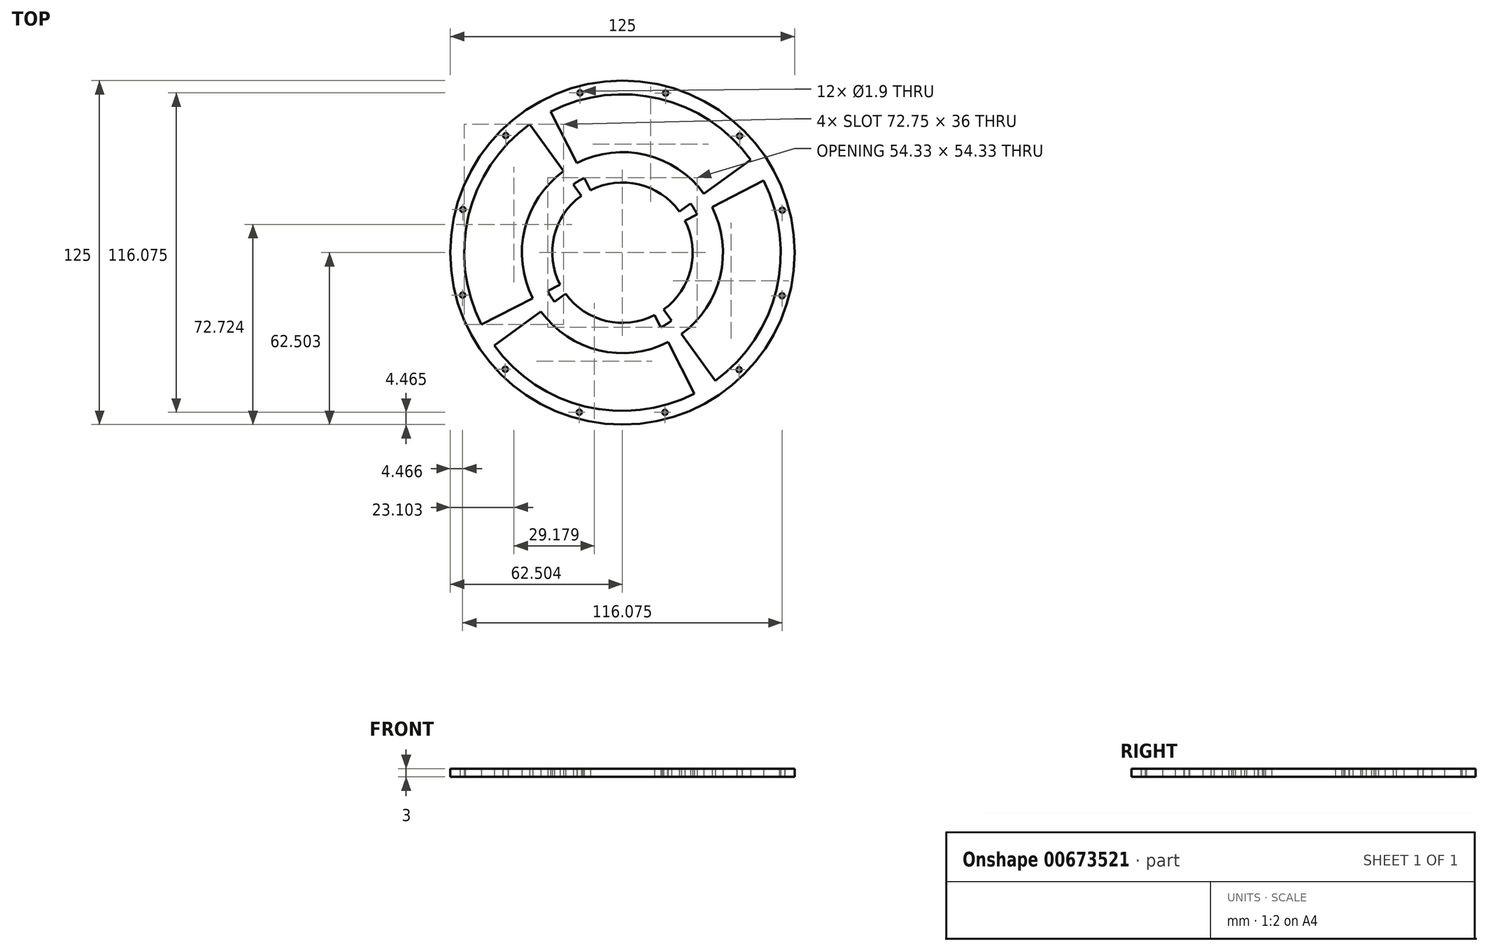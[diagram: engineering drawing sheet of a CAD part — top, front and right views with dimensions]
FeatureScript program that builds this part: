
annotation { "Feature Type Name" : "Feature", "Feature Type Description" : "" }
export const myFeature = defineFeature(function(context is Context, id is Id, definition is map)
    precondition{}
    {
        {
            var Q0;
            Q0=qCreatedBy(makeId("Top.planeOp"),FACE);
            var sketch = newSketch(context, id + "F0", { "sketchPlane" : qUnion([Q0])});
            skCircle(sketch, "E0", {"center": v(-11.5, 27.97) * mm, "radius": 25.5 * mm});
            skCircle(sketch, "E1.0", {"center": v(-11.5, 27.97) * mm, "radius": 30.5 * mm});
            skCircle(sketch, "E2", {"center": v(-11.5, 27.97) * mm, "radius": 57.5 * mm});
            skCircle(sketch, "E3.0", {"center": v(-11.5, 27.97) * mm, "radius": 62.5 * mm});
            skLineSegment(sketch, "E4", {"start": v(-11.5, 27.97) * mm, "end": v(39.71, 54.12) * mm});
            skLineSegment(sketch, "E5", {"start": v(-11.5, 27.97) * mm, "end": v(35.1, 61.67) * mm});
            skLineSegment(sketch, "E6.1.0", {"start": v(-11.5, 27.97) * mm, "end": v(-45.2, 74.57) * mm});
            skLineSegment(sketch, "E6.1.1", {"start": v(-11.5, 27.97) * mm, "end": v(-37.65, 79.18) * mm});
            skLineSegment(sketch, "E6.2.0", {"start": v(-11.5, 27.97) * mm, "end": v(-58.09, -5.72) * mm});
            skLineSegment(sketch, "E6.2.1", {"start": v(-11.5, 27.97) * mm, "end": v(-62.7, 1.82) * mm});
            skLineSegment(sketch, "E6.3.0", {"start": v(-11.5, 27.97) * mm, "end": v(22.2, -18.62) * mm});
            skLineSegment(sketch, "E6.3.1", {"start": v(-11.5, 27.97) * mm, "end": v(14.66, -23.24) * mm});
            skCircle(sketch, "E7", {"center": v(-11.5, 27.97) * mm, "radius": 36.52 * mm});
            skCircle(sketch, "E8", {"center": v(-27.16, -30) * mm, "radius": 0.95 * mm});
            skCircle(sketch, "E9.1.0", {"center": v(3.93, -30.06) * mm, "radius": 0.95 * mm});
            skCircle(sketch, "E9.2.0", {"center": v(30.88, -14.58) * mm, "radius": 0.95 * mm});
            skCircle(sketch, "E9.3.0", {"center": v(46.48, 12.31) * mm, "radius": 0.95 * mm});
            skCircle(sketch, "E9.4.0", {"center": v(46.54, 43.4) * mm, "radius": 0.95 * mm});
            skCircle(sketch, "E9.5.0", {"center": v(31.05, 70.35) * mm, "radius": 0.95 * mm});
            skCircle(sketch, "E9.6.0", {"center": v(4.17, 85.95) * mm, "radius": 0.95 * mm});
            skCircle(sketch, "E9.7.0", {"center": v(-26.92, 86.01) * mm, "radius": 0.95 * mm});
            skCircle(sketch, "E9.8.0", {"center": v(-53.87, 70.52) * mm, "radius": 0.95 * mm});
            skCircle(sketch, "E9.9.0", {"center": v(-69.47, 43.63) * mm, "radius": 0.95 * mm});
            skCircle(sketch, "E9.10.0", {"center": v(-69.53, 12.55) * mm, "radius": 0.95 * mm});
            skCircle(sketch, "E9.11.0", {"center": v(-54.05, -14.4) * mm, "radius": 0.95 * mm});
            skSolve(sketch);
        }
        {
            var Q0;
            Q0=qSketchRegion(id+"F0",true);
            var Q1;
            {var subQ0=sQuery(id+"F0.wireOp",EDGE,"E5");var subQ1=sQuery(id+"F0.wireOp",EDGE,"E0");var subQ2=makeQuery(id+"F0.imprint","INTERSECT",VERTEX,{"derivedFrom":[subQ1,subQ0]});Q1=makeQuery(id+"F0.imprint","IMPRINT",FACE,{"disambiguationData":[TD([[makeQuery(id+"F0.imprint","IMPRINT",EDGE,{"disambiguationData":[TD([[subQ2,-1.0]])],"derivedFrom":subQ1}),-1.0]])]});}
            var Q2;
            {var subQ0=sQuery(id+"F0.wireOp",EDGE,"E6.1.0");var subQ1=sQuery(id+"F0.wireOp",EDGE,"E0");var subQ2=makeQuery(id+"F0.imprint","INTERSECT",VERTEX,{"derivedFrom":[subQ1,subQ0]});Q2=makeQuery(id+"F0.imprint","IMPRINT",FACE,{"disambiguationData":[TD([[makeQuery(id+"F0.imprint","IMPRINT",EDGE,{"disambiguationData":[TD([[subQ2,-1.0]])],"derivedFrom":subQ1}),-1.0]])]});}
            var Q3;
            {var subQ0=sQuery(id+"F0.wireOp",EDGE,"E6.2.0");var subQ1=sQuery(id+"F0.wireOp",EDGE,"E0");var subQ2=makeQuery(id+"F0.imprint","INTERSECT",VERTEX,{"derivedFrom":[subQ1,subQ0]});Q3=makeQuery(id+"F0.imprint","IMPRINT",FACE,{"disambiguationData":[TD([[makeQuery(id+"F0.imprint","IMPRINT",EDGE,{"disambiguationData":[TD([[subQ2,-1.0]])],"derivedFrom":subQ1}),-1.0]])]});}
            var Q4;
            {var subQ0=sQuery(id+"F0.wireOp",EDGE,"E4");var subQ1=sQuery(id+"F0.wireOp",EDGE,"E0");var subQ2=makeQuery(id+"F0.imprint","INTERSECT",VERTEX,{"derivedFrom":[subQ1,subQ0]});Q4=makeQuery(id+"F0.imprint","IMPRINT",FACE,{"disambiguationData":[TD([[makeQuery(id+"F0.imprint","IMPRINT",EDGE,{"disambiguationData":[TD([[subQ2,1.0]])],"derivedFrom":subQ1}),-1.0]])]});}
            var Q5;
            {var subQ0=sQuery(id+"F0.wireOp",EDGE,"E5");var subQ1=sQuery(id+"F0.wireOp",EDGE,"E1.0");var subQ2=makeQuery(id+"F0.imprint","INTERSECT",VERTEX,{"derivedFrom":[subQ1,subQ0]});Q5=makeQuery(id+"F0.imprint","IMPRINT",FACE,{"disambiguationData":[TD([[makeQuery(id+"F0.imprint","IMPRINT",EDGE,{"disambiguationData":[TD([[subQ2,1.0]])],"derivedFrom":subQ1}),-1.0]])]});}
            var Q6;
            {var subQ0=sQuery(id+"F0.wireOp",EDGE,"E6.1.1");var subQ1=sQuery(id+"F0.wireOp",EDGE,"E1.0");var subQ2=makeQuery(id+"F0.imprint","INTERSECT",VERTEX,{"derivedFrom":[subQ1,subQ0]});Q6=makeQuery(id+"F0.imprint","IMPRINT",FACE,{"disambiguationData":[TD([[makeQuery(id+"F0.imprint","IMPRINT",EDGE,{"disambiguationData":[TD([[subQ2,-1.0]])],"derivedFrom":subQ1}),-1.0]])]});}
            var Q7;
            {var subQ0=sQuery(id+"F0.wireOp",EDGE,"E6.3.1");var subQ1=sQuery(id+"F0.wireOp",EDGE,"E1.0");var subQ2=makeQuery(id+"F0.imprint","INTERSECT",VERTEX,{"derivedFrom":[subQ1,subQ0]});Q7=makeQuery(id+"F0.imprint","IMPRINT",FACE,{"disambiguationData":[TD([[makeQuery(id+"F0.imprint","IMPRINT",EDGE,{"disambiguationData":[TD([[subQ2,-1.0]])],"derivedFrom":subQ1}),-1.0]])]});}
            var Q8;
            {var subQ0=sQuery(id+"F0.wireOp",EDGE,"E6.2.1");var subQ1=sQuery(id+"F0.wireOp",EDGE,"E1.0");var subQ2=makeQuery(id+"F0.imprint","INTERSECT",VERTEX,{"derivedFrom":[subQ1,subQ0]});Q8=makeQuery(id+"F0.imprint","IMPRINT",FACE,{"disambiguationData":[TD([[makeQuery(id+"F0.imprint","IMPRINT",EDGE,{"disambiguationData":[TD([[subQ2,-1.0]])],"derivedFrom":subQ1}),-1.0]])]});}
            var Q9;
            {var subQ0=sQuery(id+"F0.wireOp",EDGE,"E4");var subQ1=sQuery(id+"F0.wireOp",EDGE,"E1.0");var subQ2=makeQuery(id+"F0.imprint","INTERSECT",VERTEX,{"derivedFrom":[subQ1,subQ0]});Q9=makeQuery(id+"F0.imprint","IMPRINT",FACE,{"disambiguationData":[TD([[makeQuery(id+"F0.imprint","IMPRINT",EDGE,{"disambiguationData":[TD([[subQ2,1.0]])],"derivedFrom":subQ1}),-1.0]])]});}
            var Q10;
            {var subQ0=sQuery(id+"F0.wireOp",EDGE,"E6.2.0");var subQ1=sQuery(id+"F0.wireOp",EDGE,"E1.0");var subQ2=makeQuery(id+"F0.imprint","INTERSECT",VERTEX,{"derivedFrom":[subQ1,subQ0]});Q10=makeQuery(id+"F0.imprint","IMPRINT",FACE,{"disambiguationData":[TD([[makeQuery(id+"F0.imprint","IMPRINT",EDGE,{"disambiguationData":[TD([[subQ2,-1.0]])],"derivedFrom":subQ1}),-1.0]])]});}
            var Q11;
            {var subQ0=sQuery(id+"F0.wireOp",EDGE,"E6.1.0");var subQ1=sQuery(id+"F0.wireOp",EDGE,"E1.0");var subQ2=makeQuery(id+"F0.imprint","INTERSECT",VERTEX,{"derivedFrom":[subQ1,subQ0]});Q11=makeQuery(id+"F0.imprint","IMPRINT",FACE,{"disambiguationData":[TD([[makeQuery(id+"F0.imprint","IMPRINT",EDGE,{"disambiguationData":[TD([[subQ2,-1.0]])],"derivedFrom":subQ1}),-1.0]])]});}
            var Q12;
            {var subQ0=sQuery(id+"F0.wireOp",EDGE,"E5");var subQ1=sQuery(id+"F0.wireOp",EDGE,"E1.0");var subQ2=makeQuery(id+"F0.imprint","INTERSECT",VERTEX,{"derivedFrom":[subQ1,subQ0]});Q12=makeQuery(id+"F0.imprint","IMPRINT",FACE,{"disambiguationData":[TD([[makeQuery(id+"F0.imprint","IMPRINT",EDGE,{"disambiguationData":[TD([[subQ2,-1.0]])],"derivedFrom":subQ1}),-1.0]])]});}
            var Q13;
            {var subQ0=sQuery(id+"F0.wireOp",EDGE,"E6.2.0");var subQ1=sQuery(id+"F0.wireOp",EDGE,"E2");var subQ2=makeQuery(id+"F0.imprint","INTERSECT",VERTEX,{"derivedFrom":[subQ1,subQ0]});Q13=makeQuery(id+"F0.imprint","IMPRINT",FACE,{"disambiguationData":[TD([[makeQuery(id+"F0.imprint","IMPRINT",EDGE,{"disambiguationData":[TD([[subQ2,1.0]])],"derivedFrom":subQ1}),1.0]])]});}
            var Q14;
            {var subQ0=sQuery(id+"F0.wireOp",EDGE,"E6.3.0");var subQ1=sQuery(id+"F0.wireOp",EDGE,"E2");var subQ2=makeQuery(id+"F0.imprint","INTERSECT",VERTEX,{"derivedFrom":[subQ1,subQ0]});Q14=makeQuery(id+"F0.imprint","IMPRINT",FACE,{"disambiguationData":[TD([[makeQuery(id+"F0.imprint","IMPRINT",EDGE,{"disambiguationData":[TD([[subQ2,1.0]])],"derivedFrom":subQ1}),1.0]])]});}
            var Q15;
            {var subQ0=sQuery(id+"F0.wireOp",EDGE,"E4");var subQ1=sQuery(id+"F0.wireOp",EDGE,"E2");var subQ2=makeQuery(id+"F0.imprint","INTERSECT",VERTEX,{"derivedFrom":[subQ1,subQ0]});Q15=makeQuery(id+"F0.imprint","IMPRINT",FACE,{"disambiguationData":[TD([[makeQuery(id+"F0.imprint","IMPRINT",EDGE,{"disambiguationData":[TD([[subQ2,-1.0]])],"derivedFrom":subQ1}),1.0]])]});}
            var Q16;
            {var subQ0=sQuery(id+"F0.wireOp",EDGE,"E6.1.0");var subQ1=sQuery(id+"F0.wireOp",EDGE,"E2");var subQ2=makeQuery(id+"F0.imprint","INTERSECT",VERTEX,{"derivedFrom":[subQ1,subQ0]});Q16=makeQuery(id+"F0.imprint","IMPRINT",FACE,{"disambiguationData":[TD([[makeQuery(id+"F0.imprint","IMPRINT",EDGE,{"disambiguationData":[TD([[subQ2,1.0]])],"derivedFrom":subQ1}),1.0]])]});}
            extrude(context, id + "F1", {"entities" : qUnion([Q0, Q1, Q2, Q3, Q4, Q5, Q6, Q7, Q8, Q9, Q10, Q11, Q12, Q13, Q14, Q15, Q16]), "depth" : 3 * mm, "offsetDistance" : 25 * mm});
        }
    });
